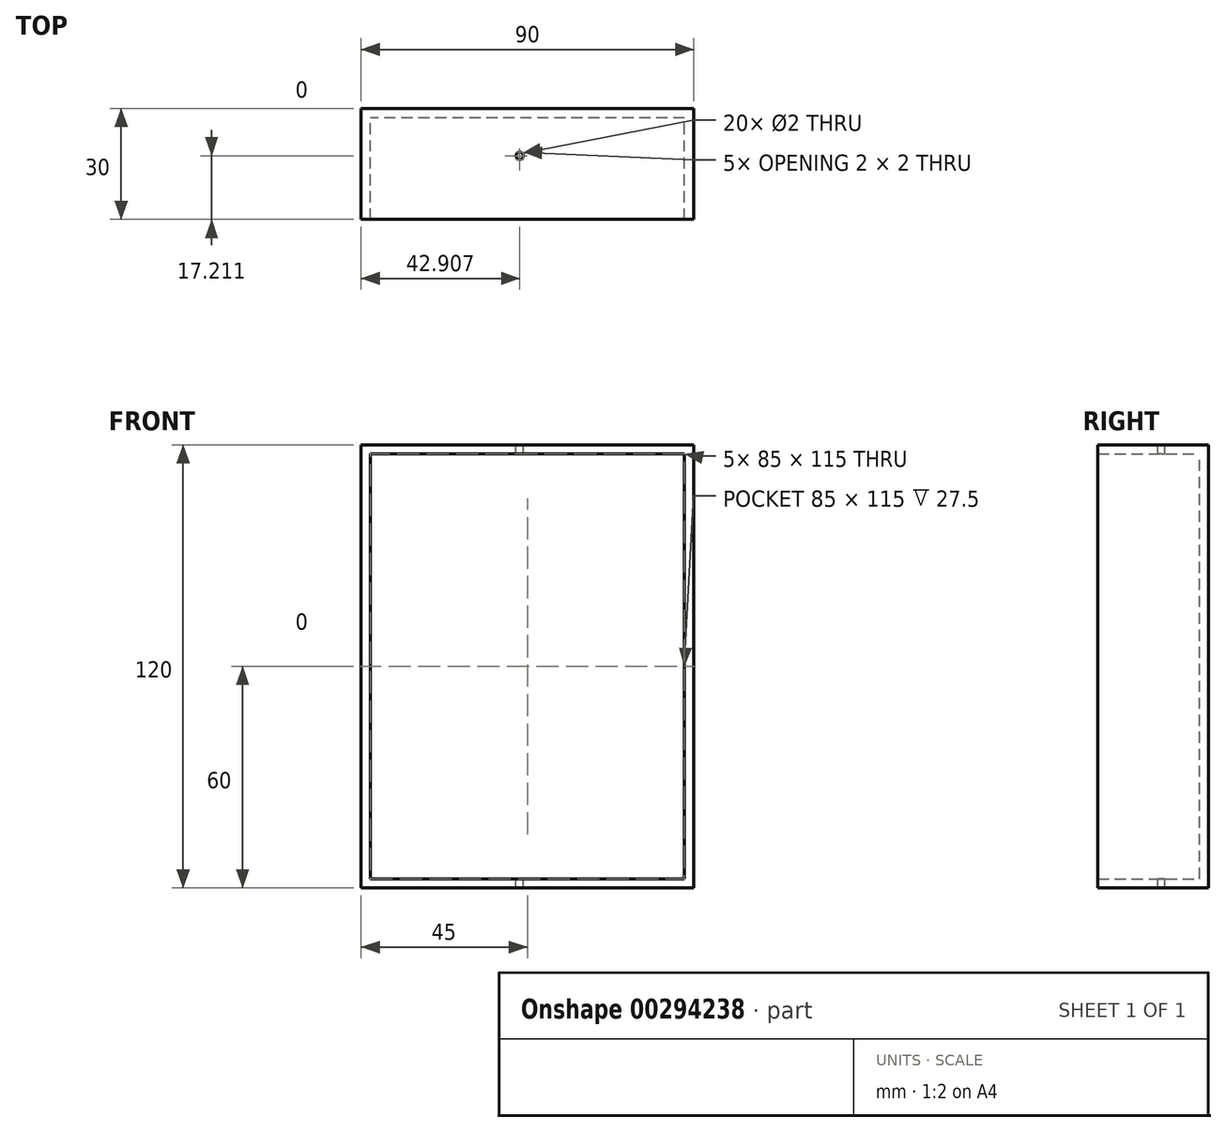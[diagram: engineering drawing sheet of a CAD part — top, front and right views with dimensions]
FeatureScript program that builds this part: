
annotation { "Feature Type Name" : "Feature", "Feature Type Description" : "" }
export const myFeature = defineFeature(function(context is Context, id is Id, definition is map)
    precondition{}
    {
        {
            var Q0;
            Q0=qCreatedBy(makeId("Front.planeOp"),FACE);
            var sketch = newSketch(context, id + "F0", { "sketchPlane" : qUnion([Q0])});
            skLineSegment(sketch, "E0.bottom", {"start": v(0, 0) * mm, "end": v(-90, 0) * mm});
            skLineSegment(sketch, "E0.top", {"start": v(0, 120) * mm, "end": v(-90, 120) * mm});
            skLineSegment(sketch, "E0.left", {"start": v(0, 0) * mm, "end": v(0, 120) * mm});
            skLineSegment(sketch, "E0.right", {"start": v(-90, 0) * mm, "end": v(-90, 120) * mm});
            skSolve(sketch);
        }
        {
            var Q0;
            Q0 = qSketchRegion(id + "F0", true);
            extrude(context, id + "F1", {"entities" : qUnion([Q0]), "depth" : 30 * mm});
        }
        {
            var Q0;
            Q0=makeQuery(id+"F1.opExtrude","CAP_FACE",FACE,{"disambiguationData":[OSD([sQuery(id+"F0.wireOp",EDGE,"E0.bottom"),sQuery(id+"F0.wireOp",EDGE,"E0.top"),sQuery(id+"F0.wireOp",EDGE,"E0.left"),sQuery(id+"F0.wireOp",EDGE,"E0.right")])],"isStart":false});
            shell(context, id + "F2", {"entities" : qUnion([Q0]), "thickness" : 2.5 * mm});
        }
        {
            var Q0;
            Q0=makeQuery(id+"F1.opExtrude","SWEPT_FACE",FACE,{"disambiguationData":[OSD([sQuery(id+"F0.wireOp",EDGE,"E0.top")])]});
            var sketch = newSketch(context, id + "F3", { "sketchPlane" : qUnion([Q0])});
            skCircle(sketch, "E1", {"center": v(-47.1, -12.79) * mm, "radius": 1 * mm});
            skSolve(sketch);
        }
        {
            var Q0;
            Q0 = qSketchRegion(id + "F3", true);
            extrude(context, id + "F4", {"entities" : qUnion([Q0]), "operationType" : NewBodyOperationType.REMOVE, "endBound" : BoundingType.THROUGH_ALL, "oppositeDirection" : true, "depth" : 25 * mm});
        }
    });
